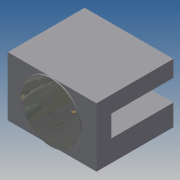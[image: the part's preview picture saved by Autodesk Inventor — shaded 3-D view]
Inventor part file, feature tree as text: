
AUTODESK INVENTOR PART (.ipt)
format: ipt  version: 2014 SP1 (Build 180222100, 222)  size: 102,912 bytes
history: native  units: in
note: dims shown in document units (in); Inventor stores cm internally (conversion verified against a paired STEP export)
features: sketch x3, extrude x2, hole x1
ambient origin geometry x8: Origin, YZ Plane, XZ Plane, XY Plane, X Axis, Y Axis, Z Axis, Center Point
bodies: Solid1 (feature_tree)
feature tree (6):
  extrude  "Extrusion1"  Depth=0.65in
  hole  "Hole1"  [1 undecoded]
  extrude  "Extrusion2"  Depth=0.01in TaperAngle=0.0deg
  sketch  "Sketch1"  dims[d0=0.5in d1=0.65in]
  sketch  "Sketch2"  dims[d2=0.75in d3=0.0in]
  sketch  "Sketch3"  dims[d4=0.13in d5=0.3in d6=0.375in d7=0.25in d8=0.5635in d9=0.3in d10=0.8108in d11=0.5in d12=0.01in d13=0.0in d14=0.125in]
note: 1 required parameter value undecoded (feature->parameter linkage not recoverable at this tier; creation-order binding heuristic only, values carry confidence <= 0.55)
